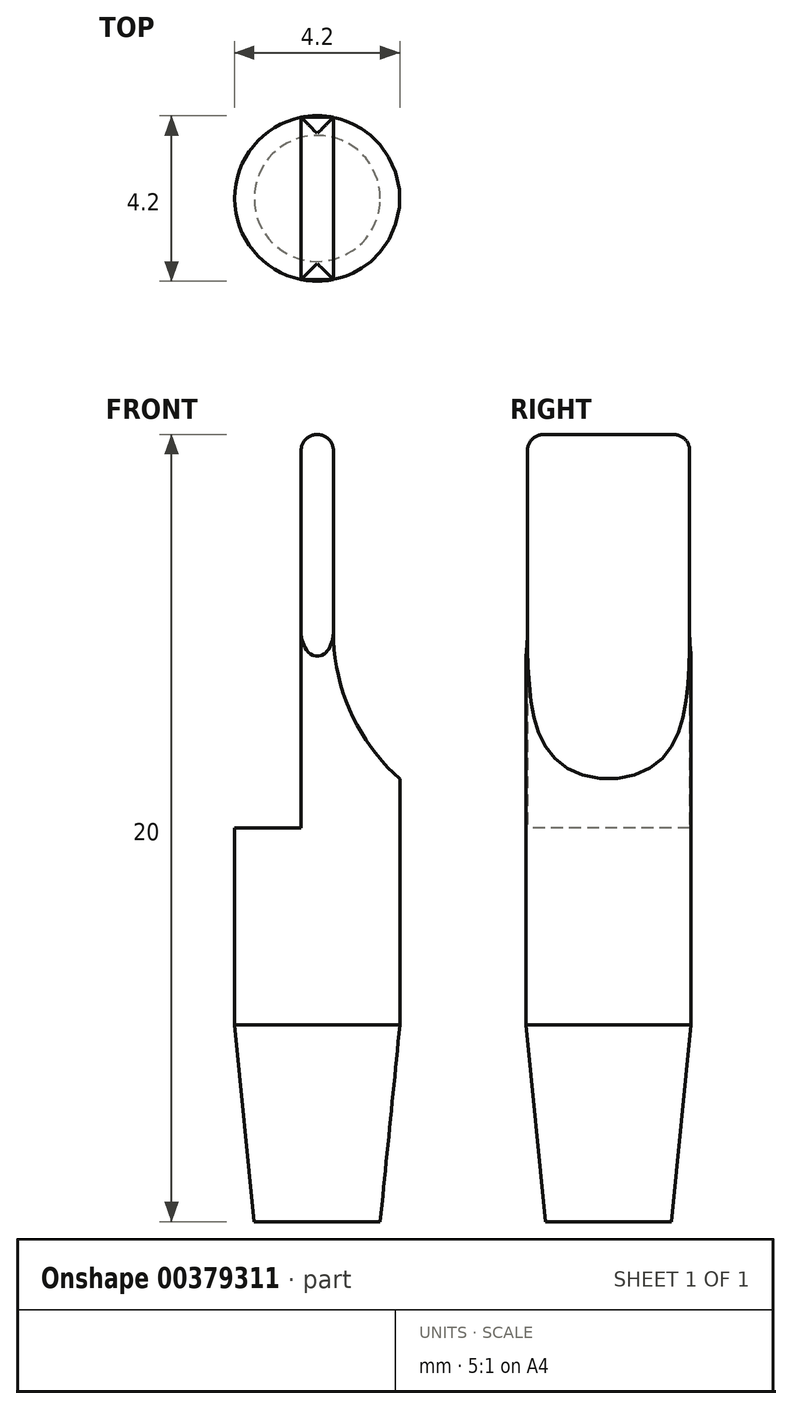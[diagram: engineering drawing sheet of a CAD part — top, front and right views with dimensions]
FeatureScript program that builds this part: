
annotation { "Feature Type Name" : "Feature", "Feature Type Description" : "" }
export const myFeature = defineFeature(function(context is Context, id is Id, definition is map)
    precondition{}
    {
        {
            var Q0;
            Q0=qCreatedBy(makeId("Top.planeOp"),FACE);
            var sketch = newSketch(context, id + "F0", { "sketchPlane" : qUnion([Q0])});
            skCircle(sketch, "E0", {"center": v(0, 0) * mm, "radius": 2.1 * mm});
            skSolve(sketch);
        }
        {
            var Q0;
            Q0 = qSketchRegion(id + "F0", true);
            extrude(context, id + "F1", {"entities" : qUnion([Q0]), "depth" : 10 * mm});
        }
        {
            var Q0;
            Q0=makeQuery(id+"F1.opExtrude","CAP_EDGE",EDGE,{"disambiguationData":[OSD([sQuery(id+"F0.wireOp",EDGE,"E0")])],"isStart":true});
            chamfer(context, id + "F2", {"entities" : qUnion([Q0]), "chamferType" : ChamferType.TWO_OFFSETS, "width1" : 5 * mm, "oppositeDirection" : false, "width2" : 0.5 * mm, "tangentPropagation" : true});
        }
        {
            var Q0;
            Q0=makeQuery(id+"F1.opExtrude","CAP_FACE",FACE,{"disambiguationData":[OSD([sQuery(id+"F0.wireOp",EDGE,"E0")])],"isStart":false});
            var sketch = newSketch(context, id + "F3", { "sketchPlane" : qUnion([Q0])});
            skLineSegment(sketch, "E1.bottom", {"start": v(-0.4, 2.06) * mm, "end": v(0.4, 2.06) * mm});
            skLineSegment(sketch, "E1.top", {"start": v(-0.4, -2.06) * mm, "end": v(0.4, -2.06) * mm});
            skLineSegment(sketch, "E1.left", {"start": v(-0.4, 2.06) * mm, "end": v(-0.4, -2.06) * mm});
            skLineSegment(sketch, "E1.right", {"start": v(0.4, 2.06) * mm, "end": v(0.4, -2.06) * mm});
            skPoint(sketch, "E1.middle", {"position": v(0, 0) * mm});
            skSolve(sketch);
        }
        {
            var Q0;
            Q0 = qSketchRegion(id + "F3", true);
            extrude(context, id + "F4", {"entities" : qUnion([Q0]), "operationType" : NewBodyOperationType.ADD, "depth" : 10 * mm});
        }
        {
            var Q0;
            Q0=makeQuery(id+"F4.opExtrude","CAP_EDGE",EDGE,{"disambiguationData":[OSD([sQuery(id+"F3.wireOp",EDGE,"E1.left")])],"isStart":true});
            var Q1;
            Q1=makeQuery(id+"F4.opExtrude","CAP_EDGE",EDGE,{"disambiguationData":[OSD([sQuery(id+"F3.wireOp",EDGE,"E1.right")])],"isStart":true});
            fillet(context, id + "F5", {"entities" : qUnion([Q0, Q1]), "radius" : 5 * mm, "tangentPropagation" : true, "allowEdgeOverflow" : false});
        }
        {
            var Q0;
            Q0=makeQuery(id+"F4.opExtrude","CAP_EDGE",EDGE,{"disambiguationData":[OSD([sQuery(id+"F3.wireOp",EDGE,"E1.bottom")])],"isStart":true});
            var Q1;
            Q1=makeQuery(id+"F4.opExtrude","CAP_EDGE",EDGE,{"disambiguationData":[OSD([sQuery(id+"F3.wireOp",EDGE,"E1.top")])],"isStart":true});
            fillet(context, id + "F6", {"entities" : qUnion([Q0, Q1]), "radius" : 5 * mm, "tangentPropagation" : true, "allowEdgeOverflow" : false});
        }
        {
            var Q0;
            Q0=makeQuery(id+"F4.opExtrude","CAP_FACE",FACE,{"disambiguationData":[OSD([sQuery(id+"F3.wireOp",EDGE,"E1.bottom"),sQuery(id+"F3.wireOp",EDGE,"E1.top"),sQuery(id+"F3.wireOp",EDGE,"E1.left"),sQuery(id+"F3.wireOp",EDGE,"E1.right")])],"isStart":false});
            fillet(context, id + "F7", {"entities" : qUnion([Q0]), "radius" : 0.4 * mm, "tangentPropagation" : true, "allowEdgeOverflow" : false});
        }
    });
